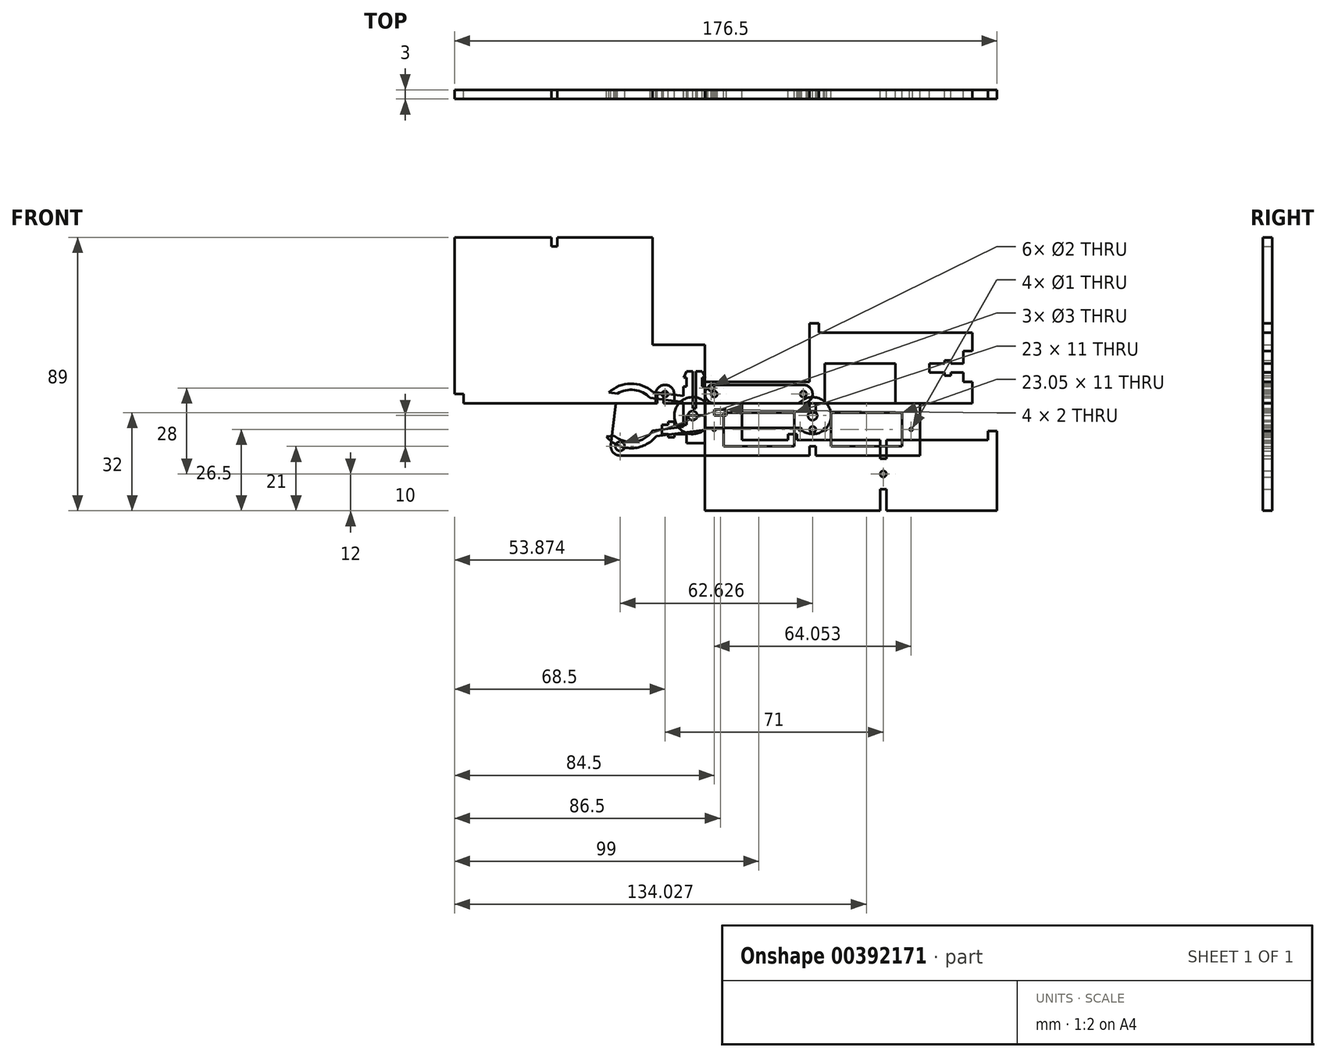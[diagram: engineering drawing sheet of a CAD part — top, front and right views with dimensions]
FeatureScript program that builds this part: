
annotation { "Feature Type Name" : "Feature", "Feature Type Description" : "" }
export const myFeature = defineFeature(function(context is Context, id is Id, definition is map)
    precondition{}
    {
        {
            var Q0;
            Q0=qCreatedBy(makeId("Front.planeOp"),FACE);
            var sketch = newSketch(context, id + "F0", { "sketchPlane" : qUnion([Q0])});
            skLineSegment(sketch, "E0", {"start": v(0, 0) * mm, "end": v(0, 19) * mm});
            skLineSegment(sketch, "E1", {"start": v(0, 19) * mm, "end": v(-17, 19) * mm});
            skLineSegment(sketch, "E2", {"start": v(-17, 54) * mm, "end": v(-17, 19) * mm});
            skLineSegment(sketch, "E3", {"start": v(-48, 54) * mm, "end": v(-17, 54) * mm});
            skLineSegment(sketch, "E4", {"start": v(-48, 54) * mm, "end": v(-48, 51) * mm});
            skLineSegment(sketch, "E5", {"start": v(-48, 51) * mm, "end": v(-50, 51) * mm});
            skLineSegment(sketch, "E6", {"start": v(-50, 51) * mm, "end": v(-50, 54) * mm});
            skLineSegment(sketch, "E7", {"start": v(-50, 54) * mm, "end": v(-81.5, 54) * mm});
            skLineSegment(sketch, "E8", {"start": v(-81.5, 54) * mm, "end": v(-81.5, 3) * mm});
            skLineSegment(sketch, "E9", {"start": v(-81.5, 3) * mm, "end": v(-78.5, 3) * mm});
            skLineSegment(sketch, "E10", {"start": v(-78.5, 3) * mm, "end": v(-78.5, 0) * mm});
            skLineSegment(sketch, "E11", {"start": v(-78.5, 0) * mm, "end": v(-15.5, 0) * mm});
            skLineSegment(sketch, "E12", {"start": v(-15.5, 0) * mm, "end": v(-15.5, 3) * mm});
            skLineSegment(sketch, "E13", {"start": v(-15.5, 3) * mm, "end": v(-13.5, 3) * mm});
            skLineSegment(sketch, "E14", {"start": v(-13.5, 3) * mm, "end": v(-13.5, 0) * mm});
            skLineSegment(sketch, "E15", {"start": v(-13.5, 0) * mm, "end": v(0, 0) * mm});
            skSolve(sketch);
        }
        {
            var Q0;
            Q0 = qSketchRegion(id + "F2", true);
            var Q1;
            Q1 = qSketchRegion(id + "F0", true);
            extrude(context, id + "F1", {"entities" : qUnion([Q0, Q1]), "depth" : 3 * mm});
        }
        {
            var Q0;
            Q0=qCreatedBy(makeId("Front.planeOp"),FACE);
            var sketch = newSketch(context, id + "F2", { "sketchPlane" : qUnion([Q0])});
            skLineSegment(sketch, "E16", {"start": v(0, 0) * mm, "end": v(34, 0) * mm});
            skLineSegment(sketch, "E17", {"start": v(34, 0) * mm, "end": v(34, -3) * mm});
            skLineSegment(sketch, "E18", {"start": v(34, -3) * mm, "end": v(36, -3) * mm});
            skLineSegment(sketch, "E19", {"start": v(36, -3) * mm, "end": v(36, 0) * mm});
            skLineSegment(sketch, "E20", {"start": v(36, 0) * mm, "end": v(70, 0) * mm});
            skLineSegment(sketch, "E21", {"start": v(70, 0) * mm, "end": v(70, -17) * mm});
            skLineSegment(sketch, "E22", {"start": v(70, -17) * mm, "end": v(36, -17) * mm});
            skLineSegment(sketch, "E23", {"start": v(36, -17) * mm, "end": v(36, -14) * mm});
            skLineSegment(sketch, "E24", {"start": v(36, -14) * mm, "end": v(34, -14) * mm});
            skLineSegment(sketch, "E25", {"start": v(34, -14) * mm, "end": v(34, -17) * mm});
            skLineSegment(sketch, "E26", {"start": v(34, -17) * mm, "end": v(0, -17) * mm});
            skLineSegment(sketch, "E27", {"start": v(0, -17) * mm, "end": v(0, 0) * mm});
            skLineSegment(sketch, "E28.bottom", {"start": v(6, -3) * mm, "end": v(29, -3) * mm});
            skLineSegment(sketch, "E28.top", {"start": v(6, -14) * mm, "end": v(29, -14) * mm});
            skLineSegment(sketch, "E28.left", {"start": v(6, -3) * mm, "end": v(6, -14) * mm});
            skLineSegment(sketch, "E28.right", {"start": v(29, -3) * mm, "end": v(29, -14) * mm});
            skLineSegment(sketch, "E29.MirrorCS", {"start": v(41, -3) * mm, "end": v(41, -14) * mm});
            skLineSegment(sketch, "E30.MirrorCS", {"start": v(64, -3) * mm, "end": v(64, -14) * mm});
            skLineSegment(sketch, "E31.MirrorCS", {"start": v(64, -3) * mm, "end": v(41, -3) * mm});
            skLineSegment(sketch, "E32.MirrorCS", {"start": v(64, -14) * mm, "end": v(41, -14) * mm});
            skCircle(sketch, "E33", {"center": v(35.03, -8.5) * mm, "radius": 1 * mm});
            skCircle(sketch, "E34", {"center": v(31, -8.5) * mm, "radius": 0.5 * mm});
            skCircle(sketch, "E35.MirrorC", {"center": v(39.05, -8.5) * mm, "radius": 0.5 * mm});
            skCircle(sketch, "E36", {"center": v(3, -8.5) * mm, "radius": 0.5 * mm});
            skCircle(sketch, "E37.MirrorC", {"center": v(67.05, -8.5) * mm, "radius": 0.5 * mm});
            skLineSegment(sketch, "E38.MirrorCS", {"start": v(64.05, -3) * mm, "end": v(41.05, -3) * mm});
            skLineSegment(sketch, "E39.MirrorCS", {"start": v(41.05, -3) * mm, "end": v(41.05, -14) * mm});
            skLineSegment(sketch, "E40.MirrorCS", {"start": v(64.05, -3) * mm, "end": v(64.05, -14) * mm});
            skLineSegment(sketch, "E41.MirrorCS", {"start": v(64.05, -14) * mm, "end": v(41.05, -14) * mm});
            skSolve(sketch);
        }
        {
            var Q0;
            Q0 = qSketchRegion(id + "F2", true);
            extrude(context, id + "F3", {"entities" : qUnion([Q0]), "depth" : 3 * mm});
        }
        {
            var Q0;
            Q0=qCreatedBy(makeId("Front.planeOp"),FACE);
            var sketch = newSketch(context, id + "F4", { "sketchPlane" : qUnion([Q0])});
            skLineSegment(sketch, "E42.bottom", {"start": v(3, 0) * mm, "end": v(32, 0) * mm});
            skLineSegment(sketch, "E42.top", {"start": v(3, 6) * mm, "end": v(32, 6) * mm});
            skLineSegment(sketch, "E42.left", {"start": v(0, 3) * mm, "end": v(0, 3) * mm});
            skLineSegment(sketch, "E42.right", {"start": v(35, 3) * mm, "end": v(35, 3) * mm});
            skPoint(sketch, "E43.visualSharp", {"position": v(0, 6) * mm});
            skArc(sketch, "E43.filletArc", {"start": v(3, 6) * mm, "mid": v(0.88, 5.12) * mm, "end": v(0, 3) * mm});
            skPoint(sketch, "E44.visualSharp", {"position": v(35, 6) * mm});
            skArc(sketch, "E44.filletArc", {"start": v(35, 3) * mm, "mid": v(34.12, 5.12) * mm, "end": v(32, 6) * mm});
            skPoint(sketch, "E45.visualSharp", {"position": v(35, 0) * mm});
            skArc(sketch, "E45.filletArc", {"start": v(32, 0) * mm, "mid": v(34.12, 0.88) * mm, "end": v(35, 3) * mm});
            skPoint(sketch, "E46.visualSharp", {"position": v(0, 0) * mm});
            skArc(sketch, "E46.filletArc", {"start": v(0, 3) * mm, "mid": v(0.88, 0.88) * mm, "end": v(3, 0) * mm});
            skCircle(sketch, "E47", {"center": v(3, 3) * mm, "radius": 1 * mm});
            skCircle(sketch, "E48", {"center": v(32, 3) * mm, "radius": 1 * mm});
            skSolve(sketch);
        }
        {
            var Q0;
            Q0 = qSketchRegion(id + "F4", true);
            extrude(context, id + "F5", {"entities" : qUnion([Q0]), "depth" : 3 * mm});
        }
        {
            var Q0;
            Q0=qCreatedBy(makeId("Front.planeOp"),FACE);
            var sketch = newSketch(context, id + "F6", { "sketchPlane" : qUnion([Q0])});
            skLineSegment(sketch, "E49", {"start": v(0, 0) * mm, "end": v(0, 7) * mm});
            skLineSegment(sketch, "E50", {"start": v(34, 7) * mm, "end": v(34, 26) * mm});
            skLineSegment(sketch, "E51", {"start": v(34, 26) * mm, "end": v(37, 26) * mm});
            skLineSegment(sketch, "E52", {"start": v(37, 26) * mm, "end": v(37, 23) * mm});
            skLineSegment(sketch, "E53", {"start": v(37, 23) * mm, "end": v(87, 23) * mm});
            skLineSegment(sketch, "E54", {"start": v(87, 23) * mm, "end": v(87, 17) * mm});
            skLineSegment(sketch, "E55", {"start": v(87, 17) * mm, "end": v(84, 17) * mm});
            skLineSegment(sketch, "E56", {"start": v(84, 13) * mm, "end": v(80, 13) * mm});
            skLineSegment(sketch, "E57", {"start": v(80, 13) * mm, "end": v(80, 14) * mm});
            skLineSegment(sketch, "E58", {"start": v(80, 14) * mm, "end": v(78, 14) * mm});
            skLineSegment(sketch, "E59", {"start": v(78, 14) * mm, "end": v(78, 13) * mm});
            skLineSegment(sketch, "E60", {"start": v(78, 13) * mm, "end": v(73, 13) * mm});
            skLineSegment(sketch, "E61", {"start": v(73, 13) * mm, "end": v(73, 10) * mm});
            skLineSegment(sketch, "E62", {"start": v(73, 10) * mm, "end": v(78, 10) * mm});
            skLineSegment(sketch, "E63", {"start": v(78, 10) * mm, "end": v(78, 9) * mm});
            skLineSegment(sketch, "E64", {"start": v(78, 9) * mm, "end": v(80, 9) * mm});
            skLineSegment(sketch, "E65", {"start": v(80, 9) * mm, "end": v(80, 10) * mm});
            skLineSegment(sketch, "E66", {"start": v(80, 10) * mm, "end": v(84, 10) * mm});
            skLineSegment(sketch, "E67", {"start": v(84, 10) * mm, "end": v(84, 7) * mm});
            skLineSegment(sketch, "E68", {"start": v(84, 7) * mm, "end": v(87, 7) * mm});
            skLineSegment(sketch, "E69", {"start": v(87, 7) * mm, "end": v(87, 0) * mm});
            skLineSegment(sketch, "E70", {"start": v(84, 17) * mm, "end": v(84, 13) * mm});
            skLineSegment(sketch, "E71", {"start": v(87, 0) * mm, "end": v(62, 0) * mm});
            skLineSegment(sketch, "E72", {"start": v(62, 0) * mm, "end": v(62, 13) * mm});
            skLineSegment(sketch, "E73", {"start": v(62, 13) * mm, "end": v(39, 13) * mm});
            skLineSegment(sketch, "E74", {"start": v(39, 13) * mm, "end": v(39, 0) * mm});
            skLineSegment(sketch, "E75", {"start": v(39, 0) * mm, "end": v(0, 0) * mm});
            skCircle(sketch, "E76", {"center": v(2.02, 5) * mm, "radius": 1 * mm});
            skLineSegment(sketch, "E77", {"start": v(0, 7) * mm, "end": v(34, 7) * mm});
            skSolve(sketch);
        }
        {
            var Q0;
            Q0 = qSketchRegion(id + "F6", true);
            extrude(context, id + "F7", {"entities" : qUnion([Q0]), "depth" : 3 * mm});
        }
        {
            var Q0;
            Q0=qCreatedBy(makeId("Front.planeOp"),FACE);
            var sketch = newSketch(context, id + "F8", { "sketchPlane" : qUnion([Q0])});
            skLineSegment(sketch, "E78", {"start": v(0, 0) * mm, "end": v(-10, 0) * mm});
            skLineSegment(sketch, "E79", {"start": v(-10, 0) * mm, "end": v(-10, 3) * mm});
            skLineSegment(sketch, "E80", {"start": v(-16, 3) * mm, "end": v(-16, 0) * mm});
            skLineSegment(sketch, "E81", {"start": v(-16, 0) * mm, "end": v(-29, 0) * mm});
            skLineSegment(sketch, "E82", {"start": v(0, 0) * mm, "end": v(0, -4) * mm});
            skLineSegment(sketch, "E83", {"start": v(0, -4) * mm, "end": v(-6, -4) * mm});
            skLineSegment(sketch, "E84", {"start": v(-6, -4) * mm, "end": v(-6, -7) * mm});
            skLineSegment(sketch, "E85", {"start": v(-6, -7) * mm, "end": v(-10, -7) * mm});
            skLineSegment(sketch, "E86", {"start": v(-10, -7) * mm, "end": v(-10, -6) * mm});
            skLineSegment(sketch, "E87", {"start": v(-10, -6) * mm, "end": v(-12, -6) * mm});
            skLineSegment(sketch, "E88", {"start": v(-12, -6) * mm, "end": v(-12, -7) * mm});
            skLineSegment(sketch, "E89", {"start": v(-12, -7) * mm, "end": v(-14, -7) * mm});
            skLineSegment(sketch, "E90", {"start": v(-14, -7) * mm, "end": v(-14, -10) * mm});
            skLineSegment(sketch, "E91", {"start": v(-14, -10) * mm, "end": v(-12, -10) * mm});
            skLineSegment(sketch, "E92", {"start": v(-12, -10) * mm, "end": v(-12, -11) * mm});
            skLineSegment(sketch, "E93", {"start": v(-12, -11) * mm, "end": v(-10, -11) * mm});
            skLineSegment(sketch, "E94", {"start": v(-10, -11) * mm, "end": v(-10, -10) * mm});
            skLineSegment(sketch, "E95", {"start": v(-10, -10) * mm, "end": v(-6, -10) * mm});
            skLineSegment(sketch, "E96", {"start": v(-6, -10) * mm, "end": v(-6, -13) * mm});
            skLineSegment(sketch, "E97", {"start": v(-6, -13) * mm, "end": v(0, -13) * mm});
            skLineSegment(sketch, "E98", {"start": v(0, -13) * mm, "end": v(0, -17) * mm});
            skLineSegment(sketch, "E99", {"start": v(0, -17) * mm, "end": v(-27.63, -17) * mm});
            skLineSegment(sketch, "E100", {"start": v(-30.6, -13.65) * mm, "end": v(-29, 0) * mm});
            skPoint(sketch, "E101.visualSharp", {"position": v(-31, -17) * mm});
            skArc(sketch, "E101.filletArc", {"start": v(-30.6, -13.65) * mm, "mid": v(-29.87, -16) * mm, "end": v(-27.63, -17) * mm});
            skLineSegment(sketch, "E102", {"start": v(-13, 6) * mm, "end": v(-13, 6) * mm});
            skPoint(sketch, "E103.visualSharp", {"position": v(-16, 6) * mm});
            skArc(sketch, "E103.filletArc", {"start": v(-13, 6) * mm, "mid": v(-15.12, 5.12) * mm, "end": v(-16, 3) * mm});
            skPoint(sketch, "E104.visualSharp", {"position": v(-10, 6) * mm});
            skArc(sketch, "E104.filletArc", {"start": v(-10, 3) * mm, "mid": v(-10.88, 5.12) * mm, "end": v(-13, 6) * mm});
            skCircle(sketch, "E105", {"center": v(-13, 3) * mm, "radius": 1 * mm});
            skCircle(sketch, "E106", {"center": v(-27.63, -14) * mm, "radius": 1.5 * mm});
            skSolve(sketch);
        }
        {
            var Q0;
            Q0 = qSketchRegion(id + "F8", true);
            extrude(context, id + "F9", {"entities" : qUnion([Q0]), "depth" : 3 * mm});
        }
        {
            var Q0;
            Q0=qCreatedBy(makeId("Front.planeOp"),FACE);
            var sketch = newSketch(context, id + "F10", { "sketchPlane" : qUnion([Q0])});
            skLineSegment(sketch, "E107", {"start": v(0, 0) * mm, "end": v(0, -35) * mm});
            skLineSegment(sketch, "E108", {"start": v(0, -35) * mm, "end": v(57, -35) * mm});
            skLineSegment(sketch, "E109", {"start": v(57, -35) * mm, "end": v(57, -28) * mm});
            skLineSegment(sketch, "E110", {"start": v(57, -28) * mm, "end": v(59, -28) * mm});
            skLineSegment(sketch, "E111", {"start": v(59, -28) * mm, "end": v(59, -35) * mm});
            skLineSegment(sketch, "E112", {"start": v(59, -35) * mm, "end": v(95, -35) * mm});
            skLineSegment(sketch, "E113", {"start": v(95, -35) * mm, "end": v(95, -9) * mm});
            skLineSegment(sketch, "E114", {"start": v(95, -9) * mm, "end": v(92, -9) * mm});
            skLineSegment(sketch, "E115", {"start": v(92, -9) * mm, "end": v(92, -12) * mm});
            skLineSegment(sketch, "E116", {"start": v(92, -12) * mm, "end": v(59, -12) * mm});
            skLineSegment(sketch, "E117", {"start": v(59, -12) * mm, "end": v(59, -18) * mm});
            skLineSegment(sketch, "E118", {"start": v(59, -18) * mm, "end": v(57, -18) * mm});
            skLineSegment(sketch, "E119", {"start": v(57, -18) * mm, "end": v(57, -12) * mm});
            skLineSegment(sketch, "E120", {"start": v(57, -12) * mm, "end": v(30, -12) * mm});
            skLineSegment(sketch, "E121", {"start": v(30, -12) * mm, "end": v(30, -10) * mm});
            skLineSegment(sketch, "E122", {"start": v(30, -10) * mm, "end": v(27, -10) * mm});
            skLineSegment(sketch, "E123", {"start": v(27, -10) * mm, "end": v(27, -12) * mm});
            skLineSegment(sketch, "E124", {"start": v(27, -12) * mm, "end": v(12, -12) * mm});
            skLineSegment(sketch, "E125", {"start": v(12, -12) * mm, "end": v(12, 0) * mm});
            skLineSegment(sketch, "E126.bottom", {"start": v(3, -2) * mm, "end": v(7, -2) * mm});
            skLineSegment(sketch, "E126.top", {"start": v(3, -4) * mm, "end": v(7, -4) * mm});
            skLineSegment(sketch, "E126.left", {"start": v(3, -2) * mm, "end": v(3, -4) * mm});
            skLineSegment(sketch, "E126.right", {"start": v(7, -2) * mm, "end": v(7, -4) * mm});
            skLineSegment(sketch, "E127", {"start": v(0, 0) * mm, "end": v(12, 0) * mm});
            skCircle(sketch, "E128", {"center": v(58, -23) * mm, "radius": 1 * mm});
            skSolve(sketch);
        }
        {
            var Q0;
            Q0 = qSketchRegion(id + "F10", true);
            extrude(context, id + "F11", {"entities" : qUnion([Q0]), "depth" : 3 * mm});
        }
        {
            var Q0;
            Q0=qCreatedBy(makeId("Front.planeOp"),FACE);
            var sketch = newSketch(context, id + "F12", { "sketchPlane" : qUnion([Q0])});
            skLineSegment(sketch, "E129", {"start": v(0.05, 8.4) * mm, "end": v(-0.95, 8.4) * mm});
            skLineSegment(sketch, "E130", {"start": v(-0.95, 10.4) * mm, "end": v(0.05, 8.4) * mm});
            skLineSegment(sketch, "E131", {"start": v(-0.95, 10.4) * mm, "end": v(-2.95, 10.4) * mm});
            skLineSegment(sketch, "E132", {"start": v(-2.95, 10.4) * mm, "end": v(-2.95, -1.6) * mm});
            skLineSegment(sketch, "E133", {"start": v(-2.95, -1.6) * mm, "end": v(-3.95, -1.6) * mm});
            skLineSegment(sketch, "E134", {"start": v(-3.95, -1.6) * mm, "end": v(-3.95, 10.4) * mm});
            skLineSegment(sketch, "E135.MirrorCS", {"start": v(-6.95, 8.4) * mm, "end": v(-6.04, 8.4) * mm});
            skLineSegment(sketch, "E136.MirrorCS", {"start": v(-5.95, 10.4) * mm, "end": v(-3.95, 10.4) * mm});
            skLineSegment(sketch, "E137.MirrorCS", {"start": v(-3.95, -1.6) * mm, "end": v(-2.95, -1.6) * mm});
            skLineSegment(sketch, "E138.MirrorCS", {"start": v(-5.95, 10.4) * mm, "end": v(-6.95, 8.4) * mm});
            skLineSegment(sketch, "E139", {"start": v(-6.04, 8.4) * mm, "end": v(-6.04, 5.4) * mm});
            skLineSegment(sketch, "E140", {"start": v(-6.04, 5.4) * mm, "end": v(-7.04, 5.4) * mm});
            skLineSegment(sketch, "E141", {"start": v(-7.04, 5.4) * mm, "end": v(-7.04, 2.4) * mm});
            skLineSegment(sketch, "E142", {"start": v(-0.95, 8.4) * mm, "end": v(-0.95, 5.4) * mm});
            skLineSegment(sketch, "E143", {"start": v(-0.95, 5.4) * mm, "end": v(0.05, 5.4) * mm});
            skLineSegment(sketch, "E144", {"start": v(0.05, 5.4) * mm, "end": v(0.05, -8.6) * mm});
            skArc(sketch, "E145", {"start": v(-32.05, -10.86) * mm, "mid": v(-23.9, -14.6) * mm, "end": v(-15.82, -10.67) * mm});
            skLineSegment(sketch, "E146", {"start": v(-7.04, 2.4) * mm, "end": v(-16.96, 3.67) * mm});
            skLineSegment(sketch, "E147", {"start": v(0.05, -8.6) * mm, "end": v(-15.82, -10.67) * mm});
            skLineSegment(sketch, "E148", {"start": v(-7.04, 0.38) * mm, "end": v(-7.04, -7.6) * mm});
            skArc(sketch, "E149", {"start": v(-29.57, -10.54) * mm, "mid": v(-22.92, -12.53) * mm, "end": v(-17, -8.9) * mm});
            skArc(sketch, "E150.trimOffspring", {"start": v(-17.87, 1.77) * mm, "mid": v(-22.94, 4.33) * mm, "end": v(-28.48, 3.13) * mm});
            skArc(sketch, "E151.trimOffspring", {"start": v(-16.96, 3.67) * mm, "mid": v(-24.15, 6.4) * mm, "end": v(-31.27, 3.49) * mm});
            skLineSegment(sketch, "E152", {"start": v(-31.27, 3.49) * mm, "end": v(-28.48, 3.13) * mm});
            skLineSegment(sketch, "E153", {"start": v(-17.87, 1.77) * mm, "end": v(-7.04, 0.38) * mm});
            skLineSegment(sketch, "E154", {"start": v(-17, -8.9) * mm, "end": v(-7.04, -7.6) * mm});
            skLineSegment(sketch, "E155", {"start": v(-32.05, -10.86) * mm, "end": v(-29.57, -10.54) * mm});
            skArc(sketch, "E156", {"start": v(-16.96, 3.67) * mm, "mid": v(-24.15, 6.39) * mm, "end": v(-31.27, 3.49) * mm});
            skArc(sketch, "E157", {"start": v(-17.87, 1.77) * mm, "mid": v(-22.94, 4.32) * mm, "end": v(-28.48, 3.13) * mm});
            skLineSegment(sketch, "E158", {"start": v(-7.04, -7.6) * mm, "end": v(-17, -8.9) * mm});
            skLineSegment(sketch, "E159", {"start": v(-29.57, -10.54) * mm, "end": v(-32.05, -10.86) * mm});
            skLineSegment(sketch, "E160", {"start": v(-15.82, -10.67) * mm, "end": v(0.05, -8.6) * mm});
            skLineSegment(sketch, "E161", {"start": v(0.05, -8.6) * mm, "end": v(0.05, 5.4) * mm});
            skLineSegment(sketch, "E162", {"start": v(0.05, 5.4) * mm, "end": v(-0.95, 5.4) * mm});
            skLineSegment(sketch, "E163", {"start": v(-0.95, 5.4) * mm, "end": v(-0.95, 8.4) * mm});
            skLineSegment(sketch, "E164", {"start": v(-0.95, 8.4) * mm, "end": v(0.05, 8.4) * mm});
            skLineSegment(sketch, "E165", {"start": v(0.05, 8.4) * mm, "end": v(-0.95, 10.4) * mm});
            skSolve(sketch);
        }
        {
            var Q0;
            Q0 = qSketchRegion(id + "F12", true);
            extrude(context, id + "F13", {"entities" : qUnion([Q0]), "depth" : 3 * mm});
        }
        {
            var Q0;
            Q0=qCreatedBy(makeId("Front.planeOp"),FACE);
            var sketch = newSketch(context, id + "F14", { "sketchPlane" : qUnion([Q0])});
            skLineSegment(sketch, "E166", {"start": v(0.47, 0) * mm, "end": v(30.53, 0) * mm});
            skLineSegment(sketch, "E167", {"start": v(30.53, -8) * mm, "end": v(0.47, -8) * mm});
            skArc(sketch, "E168", {"start": v(0.47, 0) * mm, "mid": v(-10, -4) * mm, "end": v(0.47, -8) * mm});
            skCircle(sketch, "E169", {"center": v(-4, -4) * mm, "radius": 1.5 * mm});
            skCircle(sketch, "E170.MirrorC", {"center": v(35, -4) * mm, "radius": 1.5 * mm});
            skArc(sketch, "E171.MirrorC", {"start": v(30.53, 0) * mm, "mid": v(41, -4) * mm, "end": v(30.53, -8) * mm});
            skPoint(sketch, "E172.orphan", {"position": v(0, -8) * mm});
            skSolve(sketch);
        }
        {
            var Q0;
            Q0 = qSketchRegion(id + "F14", true);
            extrude(context, id + "F15", {"entities" : qUnion([Q0]), "depth" : 3 * mm});
        }
    });
